FCSTD DOCUMENT  (FreeCAD 0.20R29177 +233 (Git))
Label: scroll_wheel
License: All rights reserved
LicenseURL: http://en.wikipedia.org/wiki/All_rights_reserved
objects: Sketcher::SketchObject×1, PartDesign::Body×1
note: 2 computed .brp shape members not serialized (recipe doc carries the construction recipe); baked Part::Feature solids carry a one-line shape summary decoded from their .brp

FEATURE [Sketcher::SketchObject] Sketch
  FullyConstrained = false
  MapMode = 5
  Placement = pos=(0,0,0) rot=(1,0,0;1.5708rad)
  Support = -> [XZ_Plane]
  sketch-geometry (10):
    g0: Circle CenterX=-17.7616 CenterY=3.06304 CenterZ=0 NormalX=0 NormalY=0 NormalZ=1 AngleXU=0 Radius=2.78479
    g1: Circle CenterX=-17.7616 CenterY=-3.06304 CenterZ=0 NormalX=0 NormalY=0 NormalZ=1 AngleXU=0 Radius=2.78479
    g2: LineSegment StartX=-17.7616 StartY=3.06304 StartZ=0 EndX=-17.7616 EndY=-3.06304 EndZ=0
    g3: GeomPoint X=-17.7616 Y=0 Z=0
    g4: LineSegment StartX=-23.0769 StartY=6.78474 StartZ=0 EndX=-5.025 EndY=6.78474 EndZ=0
    g5: LineSegment StartX=-5.025 StartY=6.78474 StartZ=0 EndX=-5.025 EndY=-6.78474 EndZ=0
    g6: LineSegment StartX=-5.025 StartY=-6.78474 StartZ=0 EndX=-23.0769 EndY=-6.78474 EndZ=0
    g7: LineSegment StartX=-23.0769 StartY=6.78474 StartZ=0 EndX=-23.0769 EndY=-6.78474 EndZ=0
    g8: GeomPoint X=-5.025 Y=0 Z=0
    g9: LineSegment StartX=-5.025 StartY=0 StartZ=0 EndX=0 EndY=0 EndZ=0
  constraints (19):
    c: Equal(g0,g1)
    c: Coincident(g2,g0)
    c: Coincident(g2,g1)
    c: Vertical(g2)
    c: Symmetric(g0,g1,g3)
    c: PointOnObject(g3,g-1)
    c: Horizontal(g4)
    c: Coincident(g5,g4)
    c: Vertical(g5)
    c: Coincident(g6,g5)
    c: Horizontal(g6)
    c: Coincident(g7,g4)
    c: Coincident(g7,g6)
    c: Vertical(g7)
    c: Symmetric(g4,g5,g8)
    c: PointOnObject(g8,g-1)
    c: Coincident(g9,g8)
    c: Coincident(g9,g-1)
    c: DistanceX(g9,g9) = 5.025
FEATURE [PartDesign::Body] Body
  Group = -> [Sketch]
  Origin = -> Origin
